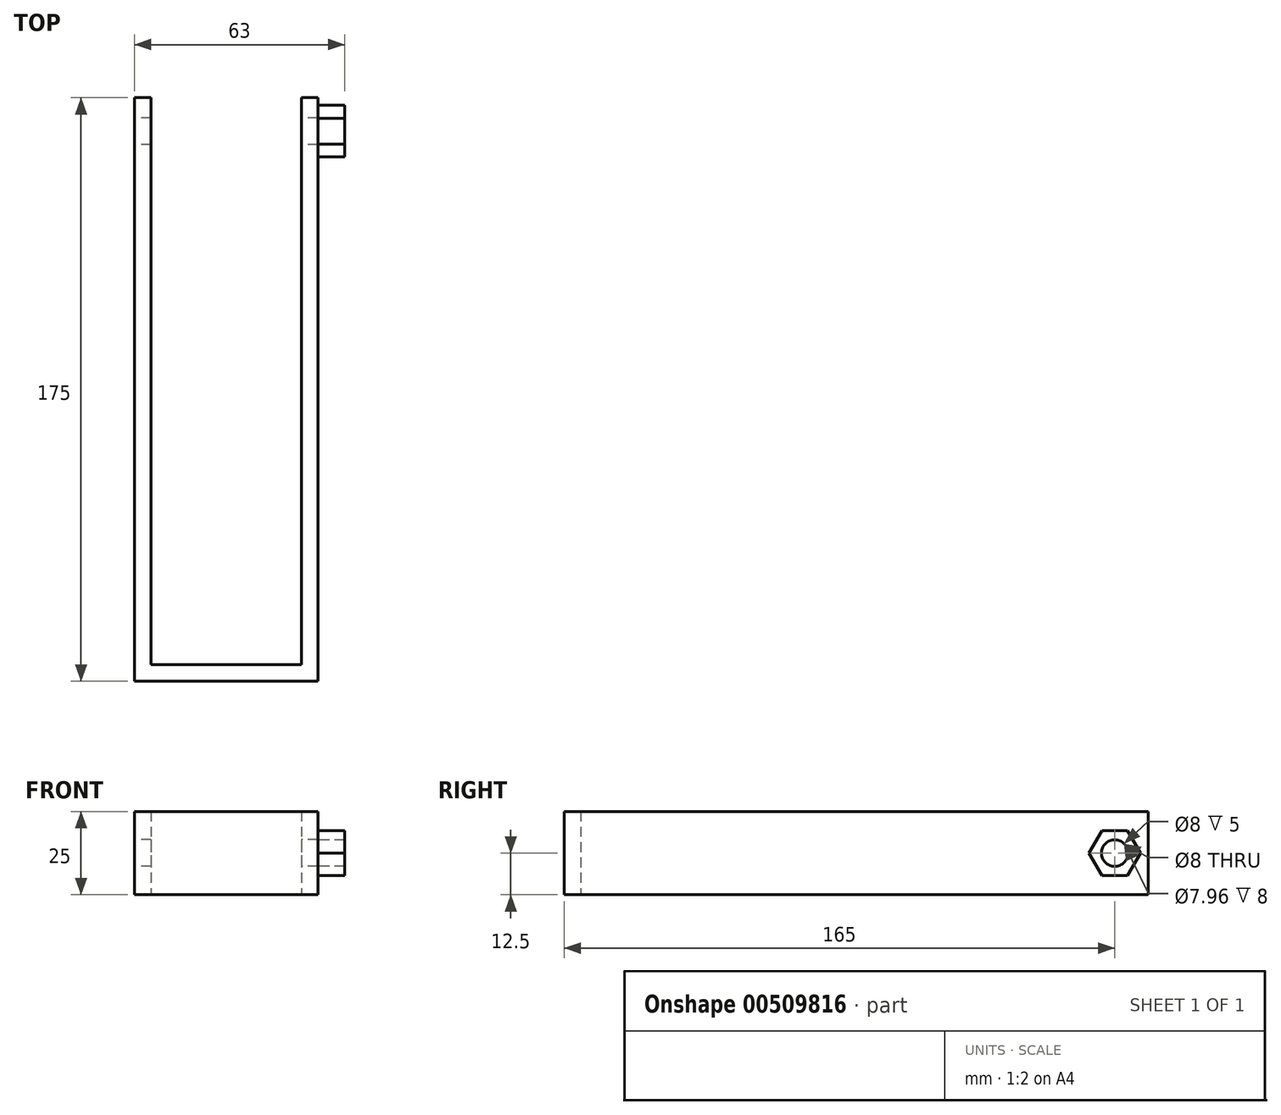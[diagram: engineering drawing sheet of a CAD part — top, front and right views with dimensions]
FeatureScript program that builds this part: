
annotation { "Feature Type Name" : "Feature", "Feature Type Description" : "" }
export const myFeature = defineFeature(function(context is Context, id is Id, definition is map)
    precondition{}
    {
        {
            var Q0;
            Q0=qCreatedBy(makeId("Top.planeOp"),FACE);
            var sketch = newSketch(context, id + "F0", { "sketchPlane" : qUnion([Q0])});
            skLineSegment(sketch, "E0", {"start": v(0, 0) * mm, "end": v(45, 0) * mm});
            skLineSegment(sketch, "E1", {"start": v(45, 0) * mm, "end": v(45, 170) * mm});
            skLineSegment(sketch, "E2", {"start": v(0, 0) * mm, "end": v(0, 170) * mm});
            skLineSegment(sketch, "E3", {"start": v(0, 170) * mm, "end": v(-5, 170) * mm});
            skLineSegment(sketch, "E4", {"start": v(-5, 170) * mm, "end": v(-5, -5) * mm});
            skLineSegment(sketch, "E5", {"start": v(-5, -5) * mm, "end": v(50, -5) * mm});
            skLineSegment(sketch, "E6", {"start": v(45, 170) * mm, "end": v(50, 170) * mm});
            skLineSegment(sketch, "E7", {"start": v(50, 170) * mm, "end": v(50, -5) * mm});
            skSolve(sketch);
        }
        {
            var Q0;
            Q0 = qSketchRegion(id + "F0", true);
            extrude(context, id + "F1", {"entities" : qUnion([Q0]), "depth" : 25 * mm});
        }
        {
            var Q0;
            Q0=makeQuery(id+"F1.opExtrude","SWEPT_FACE",FACE,{"disambiguationData":[OSD([sQuery(id+"F0.wireOp",EDGE,"E4")])]});
            var sketch = newSketch(context, id + "F2", { "sketchPlane" : qUnion([Q0])});
            skCircle(sketch, "E8", {"center": v(-160, 12.5) * mm, "radius": 4 * mm});
            skSolve(sketch);
        }
        {
            var Q0;
            Q0 = qSketchRegion(id + "F2", true);
            extrude(context, id + "F3", {"entities" : qUnion([Q0]), "operationType" : NewBodyOperationType.REMOVE, "oppositeDirection" : true, "depth" : 132.5 * mm});
        }
        {
            var Q0;
            Q0=makeQuery(id+"F1.opExtrude","SWEPT_FACE",FACE,{"disambiguationData":[OSD([sQuery(id+"F0.wireOp",EDGE,"E7")])]});
            var sketch = newSketch(context, id + "F4", { "sketchPlane" : qUnion([Q0])});
            skCircle(sketch, "E9.cCircle", {"center": v(160, 12.5) * mm, "radius": 6.68 * mm, "construction": true});
            skLineSegment(sketch, "E9.0", {"start": v(156.14, 19.18) * mm, "end": v(163.86, 19.18) * mm});
            skLineSegment(sketch, "E9.1", {"start": v(163.86, 19.18) * mm, "end": v(167.72, 12.5) * mm});
            skLineSegment(sketch, "E9.2", {"start": v(167.72, 12.5) * mm, "end": v(163.86, 5.82) * mm});
            skLineSegment(sketch, "E9.3", {"start": v(163.86, 5.82) * mm, "end": v(156.14, 5.82) * mm});
            skLineSegment(sketch, "E9.4", {"start": v(156.14, 5.82) * mm, "end": v(152.28, 12.5) * mm});
            skLineSegment(sketch, "E9.5", {"start": v(152.28, 12.5) * mm, "end": v(156.14, 19.18) * mm});
            skPoint(sketch, "E9.0.midPoint", {"position": v(160, 19.18) * mm});
            skCircle(sketch, "E10", {"center": v(160, 12.5) * mm, "radius": 3.98 * mm});
            skSolve(sketch);
        }
        {
            var Q0;
            Q0=makeQuery(id+"F4.imprint","IMPRINT",FACE,{"disambiguationData":[TD([[makeQuery(id+"F4.imprint","IMPRINT",EDGE,{"derivedFrom":sQuery(id+"F4.wireOp",EDGE,"E10")}),-1.0]])]});
            var Q1;
            Q1=makeQuery(id+"F4.imprint","IMPRINT",FACE,{"disambiguationData":[TD([[makeQuery(id+"F4.imprint","IMPRINT",EDGE,{"derivedFrom":sQuery(id+"F4.wireOp",EDGE,"E9.0")}),-1.0]])]});
            extrude(context, id + "F5", {"entities" : qUnion([Q0, Q1]), "operationType" : NewBodyOperationType.ADD, "depth" : 8 * mm});
        }
    });
